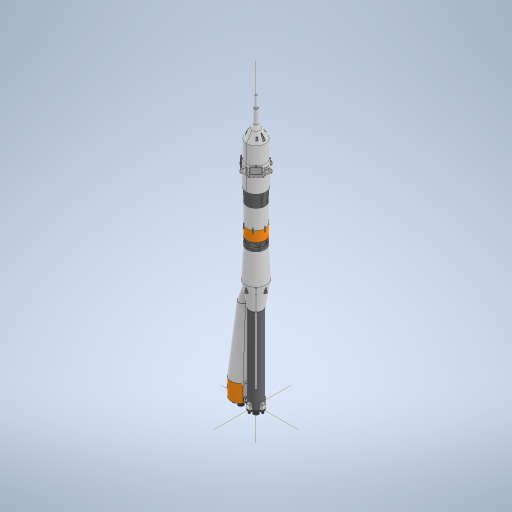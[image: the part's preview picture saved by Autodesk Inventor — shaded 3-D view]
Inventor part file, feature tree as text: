
AUTODESK INVENTOR PART (.ipt)
format: ipt  version: 2023 (Build 270158030, 158C)  size: 14,842,880 bytes
history: native  units: mm
features: fillet x71, sketch x70, extrude x63, other x23, plane x15, revolve x12, pattern_circular x11, sweep x6, mirror x3, chamfer x1, split x1
ambient origin geometry x8: Origin, YZ Plane, XZ Plane, XY Plane, X Axis, Y Axis, Z Axis, Center Point
bodies: Solid17 (feature_tree), Solid18 (feature_tree), Solid19 (feature_tree), Solid20 (feature_tree)
feature tree (276):
  other  "Soyuz Core Stage"
  extrude  "Core Airframe"  Depth=133.0mm TaperAngle=0.0deg
  extrude  "Vernier Housing"  Depth=3.4mm
  extrude  "Main Engine Extrude"  TaperAngle=0.0deg  [1 undecoded]
  extrude  "Main Engine Cut"  Depth=3.4mm
  extrude  "Vernier Nozzels"  Depth=3.4mm
  extrude  "Extrusion11"  Depth=3.4mm
  extrude  "Extrusion12"  Depth=5.5mm
  sweep  "Sweep1"
  sweep  "Booster Nosecone"
  extrude  "Extrusion16"  Depth=4.5mm
  plane  "Work Plane6"
  extrude  "Extrusion17"  Depth=4.5mm
  plane  "Work Plane5"
  extrude  "Extrusion18"  Depth=4.5mm
  fillet  "Fillet11"  Radius=4.5mm
  fillet  "Fillet12"  Radius=6.0mm
  fillet  "Fillet13"  Radius=2.0mm
  fillet  "Fillet14"  Radius=10.5mm
  extrude  "Booster Lock Extrusion"  Depth=2.0mm
  extrude  "Booster Lock Cut"  Depth=10.5mm
  other  "Work Point1"
  plane  "Work Plane1"
  sweep  "Sweep4"
  extrude  "Extrusion26"  TaperAngle=0.0deg  [1 undecoded]
  fillet  "Fillet16"  [1 undecoded]
  plane  "Work Plane4"
  other  "Work Point2"
  plane  "Work Plane2"
  extrude  "Extrusion27"  Depth=5.0mm
  extrude  "Extrusion28"  Depth=5.0mm
  extrude  "Extrusion29"  Depth=5.0mm
  fillet  "Fillet17"  [1 undecoded]
  fillet  "Fillet18"  [1 undecoded]
  fillet  "Fillet19"  [1 undecoded]
  extrude  "Extrusion30"  Depth=9.0mm
  fillet  "Fillet20"  Radius=28.0mm
  fillet  "Fillet21"  Radius=25.0mm
  fillet  "Fillet22"  [1 undecoded]
  extrude  "Extrusion31"  Depth=13.0mm
  extrude  "Extrusion32"  TaperAngle=0.0deg  [1 undecoded]
  extrude  "Extrusion33"  TaperAngle=0.0deg  [1 undecoded]
  extrude  "Extrusion34"  TaperAngle=0.0deg  [1 undecoded]
  fillet  "Fillet23"  [1 undecoded]
  fillet  "Fillet24"  Radius=17.0mm
  fillet  "Fillet25"  Radius=23.0mm
  fillet  "Fillet26"  [1 undecoded]
  extrude  "Extrusion35"  TaperAngle=0.0deg  [1 undecoded]
  extrude  "Extrusion36"  Depth=15.0mm
  extrude  "Extrusion50"  Depth=1.5mm
  fillet  "Fillet75"  [1 undecoded]
  extrude  "Extrusion51"  Depth=3.0mm TaperAngle=0.0deg
  extrude  "Extrusion52"  Depth=0.5mm TaperAngle=0.0deg
  other  "Work Point13"
  sketch  "Sketch86"  dims[d311=15.0mm d312=15.0mm]
  sweep  "Sweep6"
  revolve  "Revolution2"  [1 undecoded]
  pattern_circular  "Circular Pattern5"  [2 undecoded]
  mirror  "Mirror4"
  revolve  "Revolution3"  [1 undecoded]
  fillet  "Fillet76"  Radius=2.0mm
  fillet  "Fillet77"  Radius=21.5mm
  fillet  "Fillet78"  Radius=21.5mm
  fillet  "Fillet79"  Radius=6.2mm
  fillet  "Fillet80"  Radius=6.2mm
  fillet  "Fillet81"  Radius=0.5mm
  fillet  "Fillet82"  Radius=0.5mm
  fillet  "Fillet83"  Radius=0.5mm
  fillet  "Fillet84"  [1 undecoded]
  fillet  "Fillet85"  Radius=0.5mm
  fillet  "Fillet86"  Radius=1.3mm
  extrude  "Extrusion54"  TaperAngle=0.0deg  [1 undecoded]
  fillet  "Fillet91"  Radius=1.3mm
  fillet  "Fillet92"  Radius=3.0mm
  fillet  "Fillet93"  Radius=3.0mm
  pattern_circular  "Circular Pattern6"  [2 undecoded]
  plane  "Work Plane20"
  extrude  "Extrusion56"  TaperAngle=0.0deg  [1 undecoded]
  pattern_circular  "Circular Pattern8"  [2 undecoded]
  extrude  "Extrusion57"  Depth=1.0mm
  extrude  "Extrusion58"  Depth=0.5mm
  fillet  "Fillet94"  [1 undecoded]
  extrude  "Extrusion59"  TaperAngle=0.0deg  [1 undecoded]
  fillet  "Fillet95"  Radius=5.0mm
  pattern_circular  "Circular Pattern9"  [2 undecoded]
  extrude  "Extrusion60"  Depth=0.5mm
  fillet  "Fillet96"  [1 undecoded]
  extrude  "Extrusion61"  Depth=10.0mm TaperAngle=0.0deg
  fillet  "Fillet97"  Radius=0.5mm
  extrude  "Extrusion62"  Depth=0.5mm
  pattern_circular  "Circular Pattern11"  [2 undecoded]
  fillet  "Fillet98"  Radius=1.0mm
  extrude  "Extrusion63"  Depth=0.5mm
  fillet  "Fillet99"  Radius=0.5mm
  fillet  "Fillet100"  [1 undecoded]
  extrude  "Extrusion64"  TaperAngle=0.0deg  [1 undecoded]
  extrude  "Extrusion65"  TaperAngle=0.0deg  [1 undecoded]
  extrude  "Extrusion66"  TaperAngle=0.0deg  [1 undecoded]
  extrude  "Extrusion67"  Depth=0.5mm TaperAngle=0.0deg
  fillet  "Fillet101"  Radius=3.0mm
  plane  "Work Plane24"
  extrude  "Extrusion68"  Depth=0.5mm
  fillet  "Fillet102"  Radius=0.1mm
  extrude  "Extrusion69"  Depth=0.5mm
  pattern_circular  "Circular Pattern12"  [2 undecoded]
  extrude  "Extrusion70"  TaperAngle=0.0deg  [1 undecoded]
  fillet  "Fillet103"  [1 undecoded]
  pattern_circular  "Circular Pattern13"  [2 undecoded]
  extrude  "Extrusion71"  TaperAngle=0.0deg  [1 undecoded]
  extrude  "Extrusion72"  TaperAngle=0.0deg  [1 undecoded]
  extrude  "Extrusion73"  TaperAngle=0.0deg  [1 undecoded]
  fillet  "Fillet105"  [1 undecoded]
  extrude  "Extrusion74"  TaperAngle=0.0deg  [1 undecoded]
  extrude  "Extrusion75"  TaperAngle=0.0deg  [1 undecoded]
  fillet  "Fillet106"  [1 undecoded]
  fillet  "Fillet107"  [1 undecoded]
  other  "Work Point16"
  revolve  "Revolution6"  [1 undecoded]
  other  "Work Point17"
  plane  "Work Plane26"
  extrude  "Extrusion81"  Depth=0.5mm
  fillet  "Fillet114"  Radius=12.5mm
  fillet  "Fillet115"  Radius=12.5mm
  fillet  "Fillet116"  Radius=12.5mm
  fillet  "Fillet117"  [1 undecoded]
  mirror  "Mirror6"
  sweep  "Sweep8"
  pattern_circular  "Circular Pattern14"  [2 undecoded]
  extrude  "Extrusion80"  TaperAngle=0.0deg  [1 undecoded]
  revolve  "Revolution5"  [1 undecoded]
  extrude  "Extrusion82"  TaperAngle=0.0deg  [1 undecoded]
  fillet  "Fillet118"  [1 undecoded]
  other  "Work Point18"
  plane  "Work Plane27"
  extrude  "Extrusion83"  TaperAngle=0.0deg  [1 undecoded]
  sweep  "Sweep9"
  revolve  "Revolution7"  [1 undecoded]
  revolve  "Revolution8"  [1 undecoded]
  revolve  "Revolution9"  [1 undecoded]
  revolve  "Revolution10"  [1 undecoded]
  fillet  "Fillet119"  Radius=6.0mm
  fillet  "Fillet120"  Radius=6.0mm
  fillet  "Fillet121"  Radius=6.0mm
  fillet  "Fillet122"  [1 undecoded]
  fillet  "Fillet123"  [1 undecoded]
  fillet  "Fillet124"  Radius=5.0mm
  plane  "Work Plane30"
  extrude  "Extrusion85"  Depth=1.0mm
  extrude  "Extrusion86"  Depth=1.0mm
  extrude  "Extrusion87"  Depth=0.5mm
  extrude  "Extrusion88"  Depth=0.5mm
  fillet  "Fillet125"  Radius=1.0mm
  fillet  "Fillet126"  [1 undecoded]
  fillet  "Fillet127"  Radius=2.0mm
  fillet  "Fillet128"  [1 undecoded]
  extrude  "Extrusion89"  Depth=0.5mm
  extrude  "Extrusion90"  Depth=1.0mm
  fillet  "Fillet129"  [1 undecoded]
  fillet  "Fillet130"  Radius=1.0mm
  fillet  "Fillet131"  Radius=0.781667mm
  extrude  "Extrusion92"  Depth=0.5mm
  extrude  "Extrusion93"  Depth=0.5mm
  fillet  "Fillet134"  Radius=12.5mm
  fillet  "Fillet135"  Radius=0.5mm
  fillet  "Fillet136"  [1 undecoded]
  fillet  "Fillet138"  Radius=0.5mm
  pattern_circular  "Circular Pattern15"  [2 undecoded]
  other  "Work Point19"
  plane  "Work Plane31"
  extrude  "Extrusion94"  Depth=0.5mm
  fillet  "Fillet139"  [1 undecoded]
  revolve  "Revolution11"  [1 undecoded]
  chamfer  "Chamfer3"  Distance=1.377412mm
  fillet  "Fillet140"  Radius=1.377mm
  fillet  "Fillet141"  Radius=4.5mm
  fillet  "Fillet142"  Radius=1.0mm
  plane  "Work Plane32"
  revolve  "Revolution12"  [1 undecoded]
  fillet  "Fillet143"  Radius=4.5mm
  pattern_circular  "Circular Pattern16"  [2 undecoded]
  fillet  "Fillet144"  Radius=1.0mm
  pattern_circular  "Circular Pattern17"  [2 undecoded]
  mirror  "Mirror7"
  split  "Split1"
  sketch  "Sketch5"  dims[d0=20.0mm d1=133.0mm d2=0.0mm]
  sketch  "Sketch6"  dims[d7=0.0mm d9=3.4mm]
  sketch  "Sketch15"  dims[d10=3.4mm d12=0.0mm]
  sketch  "Sketch16"  dims[d15=3.4mm d18=3.4mm]
  other  "Soyuz Booster"
  sketch  "Sketch28"  dims[d20=3.4mm d21=3.4mm]
  sketch  "Sketch29"  dims[d25=3.4mm d26=3.4mm]
  sketch  "Sketch31"  dims[d33=7.0mm d34=0.0mm d47=5.5mm]
  sketch  "Sketch34"  dims[d48=5.5mm d49=5.5mm]
  sketch  "Sketch35"  dims[d50=5.5mm d52=4.5mm]
  sketch  "Sketch42"  dims[d57=4.5mm d58=4.5mm d59=4.5mm d60=6.0mm d61=2.094395mm d62=2.0mm d63=10.5mm]
  sketch  "Sketch43"  dims[d64=2.0mm d65=2.0mm]
  sketch  "Sketch45"  dims[d66=2.0mm d67=10.5mm]
  sketch  "Sketch51"  dims[d68=10.5mm d69=10.5mm]
  sketch  "Sketch52"  dims[d70=0.0mm d71=0.0mm d72=0.0mm]
  sketch  "Sketch53"  dims[d73=0.0mm d74=5.0mm d75=1.396263mm]
  sketch  "Sketch54"  dims[d76=5.0mm d77=5.0mm]
  sketch  "Sketch55"  dims[d78=5.0mm d79=5.0mm d80=0.0mm d81=0.0mm d82=0.0mm]
  sketch  "Sketch56"  dims[d83=0.0mm d85=9.0mm d86=-1.396263mm d156=28.0mm d160=25.0mm d161=0.0mm]
  other  "Core Stage Part 2"
  sketch  "Sketch57"  dims[d166=13.0mm d167=13.0mm d168=13.0mm d171=13.0mm]
  sketch  "Sketch81"  dims[d174=27.0mm d175=0.0mm d177=0.0mm]
  sketch  "Sketch82"  dims[d178=0.0mm d179=0.0mm]
  sketch  "Sketch83"  dims[d180=38.0mm d181=1.658063mm d236=0.0mm d237=0.0mm d278=17.0mm d280=23.0mm d281=-0.610865mm d282=0.0mm]
  other  "Interstage 1"
  sketch  "Sketch85"  dims[d304=0.0mm d309=0.0mm]
  other  "Srf3"
  sketch  "3D Sketch5"
  other  "Project to Surface5"
  sketch  "Sketch87"  dims[d313=19.0mm d314=1.5mm d316=-2.356194mm d317=0.0mm]
  other  "Project to Surface7"
  sketch  "Sketch88"  dims[d318=0.0mm d330=3.0mm d331=0.0mm]
  sketch  "Sketch89"  dims[d334=0.5mm d335=0.0mm d338=0.5mm d339=0.0mm]
  sketch  "Sketch91"  dims[d342=3.0mm d343=3.0mm]
  plane  "Work Plane19"
  sketch  "Sketch93"  dims[d344=3.0mm d345=6.0mm]
  sketch  "Sketch94"  dims[d346=1.2mm]
  other  "Interstage 2"
  sketch  "Sketch95"  dims[d347=1.2mm]
  other  "2nd Stage"
  sketch  "Sketch96"  dims[d348=1.2mm]
  sketch  "Sketch97"  dims[d349=1.2mm]
  sketch  "Sketch100"  dims[d350=0.0mm]
  other  "Srf4"
  sketch  "Sketch103"  dims[d351=0.0mm]
  sketch  "Sketch104"  dims[d352=0.0mm]
  sketch  "Sketch105"  dims[d353=0.0mm]
  sketch  "Sketch107"  dims[d354=14.5mm]
  sketch  "Sketch108"  dims[d355=14.5mm]
  sketch  "Sketch109"  dims[d356=14.5mm]
  sketch  "Sketch111"  dims[d357=14.5mm]
  sketch  "Sketch112"  dims[d358=11.5mm d359=1.745329mm]
  sketch  "Sketch113"  dims[d361=2.2mm]
  sketch  "Sketch114"  dims[d362=1.6mm]
  sketch  "Sketch115"  dims[d363=0.0mm]
  sketch  "Sketch116"  dims[d364=4.1mm d365=-1.745329mm]
  other  "2nd Stage Part 2"
  sketch  "Sketch117"  dims[d366=0.0mm]
  sketch  "Sketch118"  dims[d367=1.6mm]
  sketch  "Sketch120"  dims[d368=2.2mm]
  sketch  "Sketch121"  dims[d369=0.0mm]
  sketch  "Sketch128"  dims[d370=1.6mm]
  other  "Fairing"
  sketch  "Sketch130"  dims[d371=2.2mm]
  sketch  "Sketch132"  dims[d372=1.6mm]
  sketch  "Sketch134"  dims[d373=0.0mm]
  sketch  "Sketch135"  dims[d374=2.2mm]
  sketch  "Sketch139"  dims[d397=5.5mm d398=4.5mm d400=5.5mm d401=4.5mm d402=4.5mm d403=5.5mm d404=4.5mm d406=5.5mm d410=2.094395mm d411=6.0mm]
  sketch  "Sketch140"  dims[d412=5.0mm d413=0.0mm d414=5.0mm d415=0.0mm d416=0.0mm d417=5.0mm d418=0.0mm d419=5.0mm d421=-1.396263mm d422=9.0mm]
  other  "Escape Tower"
  plane  "Work Plane28"
  plane  "Work Plane29"
  other  "Grid Fins"
  sketch  "Sketch145"  dims[d423=0.0mm]
  sketch  "Sketch146"  dims[d424=0.0mm]
  sketch  "Sketch149"  dims[d425=0.0mm]
  sketch  "Sketch150"  dims[d426=0.0mm]
  sketch  "Sketch152"  dims[d427=9.0mm]
  sketch  "Sketch153"  dims[d428=9.0mm]
  sketch  "Sketch154"  dims[d429=9.0mm]
  sketch  "Sketch156"  dims[d430=9.0mm]
  sketch  "Sketch157"  dims[d431=6.0mm]
  other  "Pattern of Fairing:1"
  other  "Pattern of Grid Fins:2"
  sketch  "Sketch159"  dims[d432=0.0mm d446=1.396263mm d447=5.0mm d449=2.0mm d450=2.0mm d452=21.5mm d453=21.5mm d454=6.2mm d455=6.2mm d456=0.5mm d459=0.5mm d460=0.5mm d461=0.0mm d464=0.5mm d465=1.3mm d466=0.0mm d467=1.3mm d468=3.0mm d470=3.0mm d472=0.0mm d473=0.0mm d475=6.0mm d476=1.0mm d477=6.0mm d478=0.0mm d479=-0.202458mm d480=0.0mm d481=5.0mm d482=2.0mm d483=2.0mm d484=0.0mm d485=10.0mm d486=0.0mm d487=0.5mm d489=3.0mm d490=1.0mm d491=1.0mm d492=28.0mm d493=0.5mm d494=0.0mm d518=0.0mm d521=0.0mm d522=0.0mm d524=0.0mm d525=0.5mm d526=0.0mm d527=3.0mm d528=3.0mm d529=0.1mm d530=20.0mm d531=7.0mm d532=0.0mm d538=0.0mm d539=0.0mm d540=0.0mm d541=0.0mm d542=0.0mm d543=0.0mm d544=0.0mm d545=0.0mm d546=0.0mm d547=0.0mm d548=0.0mm d549=0.0mm d550=12.5mm d551=12.5mm d553=12.5mm d554=12.5mm d556=0.0mm d557=0.0mm d561=0.0mm d562=0.0mm d563=0.0mm d564=0.0mm d566=0.0mm d567=0.0mm d568=0.0mm d571=0.0mm d572=0.0mm d573=0.0mm d575=6.0mm d576=6.0mm d577=6.0mm d578=6.0mm d579=0.0mm d581=0.0mm d582=5.0mm d583=-6.108652mm d584=1.0mm d585=1.0mm d593=2.0mm d594=3.0mm d604=1.0mm d608=0.0mm d609=2.0mm d610=0.0mm d611=3.0mm d612=1.0mm d614=0.0mm d617=1.0mm d618=0.781667mm d619=2.5mm d649=12.5mm d650=12.5mm d651=0.5mm d652=0.0mm d653=0.5mm d654=4.5mm d655=4.5mm d657=0.0mm d658=1.0mm d659=1.377412mm d660=1.377mm d661=4.5mm d662=1.0mm d663=0.5mm d664=0.0mm d665=4.5mm d666=1.377mm d667=1.0mm d668=4.5mm d669=1.377mm d670=1.0mm d671=0.5mm d672=0.0mm d673=4.5mm d674=1.377mm d675=4.5mm d676=1.377mm d677=1.0mm d678=1.0mm d679=0.5mm d680=0.0mm d681=4.5mm d682=4.5mm d683=1.377mm d684=1.377mm d685=1.0mm d686=1.0mm d687=0.5mm d688=0.0mm d689=0.5mm d690=0.2mm d691=0.3mm d692=1.0mm d694=0.0mm d695=0.0mm d696=0.1mm d697=5.0mm d698=0.0mm d699=0.0mm d700=0.0mm d702=50.0mm d703=-0.541052mm d709=0.0mm d993=0.0mm d994=0.0mm d995=2.5mm d996=5.0mm d997=0.0mm d998=8.0mm d999=0.0mm d1000=0.0mm d1001=0.0mm d1002=0.0mm d1003=0.0mm d1004=0.0mm d1005=4.0mm d1006=0.0mm d1007=0.0mm d1008=0.0mm d1009=0.0mm d1010=0.0mm d1011=0.0mm d1012=0.0mm d1013=4.1mm d1014=0.0mm d1026=45.0deg d1030=0.0mm d1031=0.0mm d1034=10.0mm d1035=3.0mm d1036=0.0mm d1037=0.0mm d1038=0.1mm d1039=0.0mm d1040=2.5mm d1041=2.5mm d1042=0.9mm d1048=2.5mm d1049=2.6mm d1050=90.0deg d1051=60.0mm d1052=360.0deg d1054=1.5mm d1057=0.4mm d1058=90.0deg d1059=0.2mm d1060=0.7mm d1061=0.4mm d1062=1.0mm d1063=0.5mm d1064=0.2mm d1065=0.2mm d1066=0.2mm d1067=0.2mm d1068=0.2mm d1069=0.2mm d1070=0.1mm d1083=0.5mm d1084=0.3mm d1085=2.0mm d1086=0.0mm d1087=1.3mm d1088=0.0mm d1089=0.7mm d1090=0.5mm d1091=0.7mm d1092=60.0mm d1093=360.0deg d1103=-1.0mm d1104=0.0mm d1105=0.0mm d1106=0.0mm d1107=0.0mm d1108=30.0mm d1109=1.25mm d1110=1.4mm d1111=0.0mm d1112=1.25mm d1116=40.0mm d1117=360.0deg d1119=0.0mm d1120=0.0mm d1121=0.0mm d1122=0.0mm d1123=0.0mm d1124=0.0mm d1125=16.0mm d1126=0.0mm d1127=0.0mm d1128=0.0mm d1129=0.0mm d1130=30.0mm d1131=0.0mm d1132=0.1mm d1133=1.7mm d1134=14.0mm d1135=5.0mm d1136=0.0mm d1137=0.8mm d1138=60.0mm d1139=360.0deg d1141=0.0mm d1142=3.0mm d1143=0.0mm d1144=0.5mm d1145=1.0mm d1146=6.0mm d1147=0.0mm d1148=8.0mm d1149=0.0mm d1150=3.0mm d1151=9.0mm d1152=6.981317mm d1153=9.6mm d1154=90.0deg d1193=3.5mm d1194=1.2mm d1195=0.0mm d1196=2.5mm d1197=1.8mm d1200=2.0mm d1201=10.0mm d1203=0.3mm d1204=0.2mm d1205=9.397169mm d1206=1.165699mm d1207=1.2mm d1208=2.0mm d1209=2.0mm d1210=0.0mm d1211=60.0mm d1212=360.0deg d1214=8.0mm d1215=0.0mm d1216=0.0mm d1217=20.0mm d1218=2.0mm d1219=0.0mm d1220=0.2mm d1221=0.2mm d1222=5.5mm d1223=4.5mm d1224=4.5mm d1228=5.0mm d1229=4.0mm d1230=2.094395mm d1231=-2.094395mm d1232=0.0mm d1233=0.0mm d1234=0.0mm d1235=5.0mm d1236=4.014257mm d1238=0.0mm d1239=0.0mm d1240=1.5mm d1241=10.5mm d1242=-1.396263mm d1243=2.0mm d1244=8.5mm d1245=0.0mm d1246=4.0mm d1247=1.745329mm d1248=0.8mm d1249=1.5mm d1250=3.0mm d1251=8.5mm d1252=2.8mm d1253=0.0mm d1254=1.4mm d1258=6.8mm d1259=0.872665mm d1260=0.0mm d1261=0.0mm d1262=0.0mm d1263=0.0mm d1264=0.55mm d1265=0.0mm d1266=40.0mm d1267=360.0deg d1270=0.0mm d1271=0.0mm d1272=0.0mm d1273=3.55mm d1274=0.0mm d1275=0.8mm d1276=60.0mm d1277=360.0deg d1282=20.0mm d1283=0.349066mm d1286=4.0mm d1287=0.0mm d1288=0.2mm d1289=1.0mm d1290=0.0mm d1291=0.2mm d1292=3.5mm d1293=5.0mm d1294=7.0mm d1295=0.0mm d1296=5.0mm d1297=5.0mm d1298=0.0mm d1299=1.0mm d1300=1.0mm d1310=0.0mm d1311=0.0mm d1313=11.5mm d1316=0.3mm d1317=0.3mm d1318=3.066164mm d1319=2.367748mm d1320=9.41mm d1321=4.705mm d1324=1.81mm d1330=0.0mm d1331=0.0mm d1333=3.0mm d1361=20.0mm d1362=360.0deg d1372=0.0mm d1375=0.0mm d1391=1.0mm d1392=1.3mm d1393=2.0mm d1394=2.0mm d1395=2.0mm d1396=2.0mm d1397=1.0mm d1398=1.0mm d1399=1.0mm d1400=1.0mm d1401=1.0mm d1402=1.0mm d1403=13.566164mm d1404=12.266164mm d1405=13.566164mm d1406=12.266164mm d1407=13.566164mm d1408=12.266164mm d1409=13.566164mm d1410=12.266164mm d1411=2.0mm d1412=90.0deg d1413=1.2mm d1414=2.5mm d1417=3.0mm d1418=0.0mm d1424=3.0mm d1425=15.53343mm d1429=180.0deg d1430=23.0mm d1431=12.2mm d1432=45.0deg d1433=2.5mm d1434=2.5mm d1435=3.4mm d1436=3.4mm d1437=0.0mm d1438=0.0mm d1439=1.3mm d1440=0.0mm d1441=0.5mm d1442=0.4mm d1443=0.4mm d1444=0.4mm d1445=11.586164mm d1446=0.0mm d1447=0.0mm d1448=0.0mm d1449=0.0mm d1452=0.0mm d1453=1.3mm d1454=0.0mm d1455=0.0mm d1456=0.0mm d1458=13.566164mm d1459=12.266164mm d1460=12.266164mm d1461=13.566164mm d1462=2.0mm d1463=1.5mm d1464=0.0mm d1465=0.1mm d1469=5.0mm d1470=5.0mm d1471=20.0mm d1473=1.071mm d1474=0.0mm d1475=0.0mm d1476=0.0mm d1477=0.0mm d1478=0.0mm d1479=0.0mm d1482=19.3mm d1483=0.0mm d1484=16.057029mm d1485=3.0mm d1486=0.0mm d1487=0.0mm d1490=0.0mm d1497=15.184364mm d1498=15.0mm d1499=180.0deg d1500=27.0mm d1501=15.620697mm d1502=180.0deg d1504=60.0deg d1513=13.856406mm d1514=180.0deg d1528=14.0mm d1529=3.579724mm d1531=1.0mm d1532=1.000457mm d1533=0.917096mm d1534=1.0mm d1540=2.0mm d1541=1.329428mm d1543=1.5mm d1545=4.997278mm d1546=0.0mm d1547=3.0mm d1552=2.7mm d1554=30.892328mm d1555=2.0mm d1556=3.250296mm d1557=6.497278mm d1560=0.0mm d1561=21.46755mm d1562=25.0mm d1563=1.5mm d1564=0.0mm d1566=20.071286mm d1567=37.0mm d1568=1.0mm d1569=1.0mm d1570=27.0mm d1571=45.0mm d1572=90.0deg d1574=0.917096mm d1575=0.4mm d1576=0.4mm d1577=0.4mm d1578=0.1mm d1579=0.1mm d1580=0.2mm d1583=2.0mm d1593=1.0mm d1594=1.0mm d1596=0.5mm d1597=2.5mm d1598=3.5mm d1599=3.5mm d1600=3.5mm d1601=2.0mm d1602=0.0mm d1603=0.7mm d1604=0.7mm d1605=4.0mm d1606=0.7mm d1607=0.7mm d1608=0.0mm d1609=0.0mm d1610=0.0mm d1611=0.0mm d1612=0.0mm d1613=0.3mm d1614=0.0mm d1615=0.2mm d1616=2.0mm d1617=1.0mm d1618=2.0mm d1619=1.0mm d1621=100.0mm d1622=2.0mm d1623=2.0mm d1624=2.0mm d1625=0.0mm d1626=0.0mm d1627=0.9mm d1628=0.1mm d1629=0.1mm d1630=0.1mm d1632=1.0mm d1633=0.75mm d1634=0.75mm d1635=0.0mm d1636=0.0mm d1640=7.0mm d1641=7.0mm d1642=3.5mm d1643=0.7mm d1644=6.0mm d1645=0.0mm d1646=2.0mm d1649=0.0mm d1650=2.0mm d1651=2.25mm d1652=4.5mm d1653=0.0mm d1654=0.0mm d1655=4.0mm d1656=1.0mm d1657=0.5mm d1667=1.0mm d1668=0.0mm d1669=0.0mm d1670=0.0mm d1674=0.8mm d1676=0.8mm d1677=0.5mm d1678=0.5mm d1679=1.5mm d1680=1.7mm d1681=0.0mm d1682=2.0mm d1683=0.2mm d1684=0.1mm d1686=0.1mm d1687=20.0mm d1688=90.0deg d1690=3.5mm d1691=0.0mm d1692=4.5mm d1693=4.5mm d1694=0.0mm d1695=2.0mm d1696=0.0mm d1697=1.0mm d1698=4.0mm d1699=2.0mm d1700=45.0deg d1701=12.0mm d1702=3.0mm d1703=10.7mm d1705=5.0mm d1706=12.0mm d1707=2.443461mm d1708=1.0mm d1709=2.0mm d1710=45.0deg d1711=0.5mm d1712=0.5mm d1713=0.5mm d1714=4.5mm d1715=5.5mm d1716=8.0mm d1717=8.5mm d1718=9.424778mm d1719=3.3mm d1720=2.3mm d1721=1.745329mm d1722=0.5mm d1723=20.0mm d1724=19.198622mm d1726=0.5mm d1731=0.5mm d1732=0.5mm d1733=0.5mm d1734=0.5mm d1735=0.5mm d1736=0.5mm d1737=0.5mm d1738=0.5mm d1739=0.5mm d1740=0.5mm d1741=0.5mm d1742=0.5mm d1743=0.5mm d1744=0.5mm d1745=0.5mm d1746=0.5mm d1747=0.5mm d1748=0.5mm d1749=0.5mm d1755=0.5mm d1756=0.5mm d1757=0.5mm d1758=0.5mm d1759=0.5mm d1760=0.5mm d1763=0.5mm d1764=0.5mm d1766=0.5mm d1767=0.5mm d1768=0.5mm d1769=0.5mm d1770=0.5mm d1771=0.5mm d1772=0.5mm d1773=0.5mm d1774=0.5mm d1775=0.5mm d1776=0.5mm d1777=0.5mm d1778=0.5mm d1779=0.5mm d1780=0.5mm d1781=0.5mm d1782=0.5mm d1783=0.5mm d1784=0.5mm d1785=0.5mm d1786=0.5mm d1787=0.5mm d1788=0.5mm d1789=0.5mm d1790=0.5mm d1791=0.5mm d1792=0.5mm d1793=0.5mm d1794=20.0mm d1795=90.0deg d194=0.5mm d195=0.872665mm d196=0.5mm d197=0.872665mm d261=0.5mm d262=0.872665mm d263=0.5mm d264=0.872665mm d808=0.5mm d809=0.872665mm d810=0.5mm d811=0.872665mm d1255=0.872665mm d1351=0.5mm d1352=0.872665mm d1353=0.5mm d1354=0.872665mm]
  extrude  "Extrusion23"  Depth=0.5mm
  extrude  "Extrusion24"  Depth=1.0mm
  extrude  "Extrusion25"  Depth=0.5mm TaperAngle=0.0deg
  revolve  "RevolutionSrf2"  [1 undecoded]
  revolve  "RevolutionSrf3"  [1 undecoded]
  sketch  "Sketch39"  dims[d53=4.5mm d54=4.5mm]
  sketch  "Sketch40"  dims[d55=4.5mm d56=4.5mm]
note: 80 required parameter values undecoded (feature->parameter linkage not recoverable at this tier; creation-order binding heuristic only, values carry confidence <= 0.55)